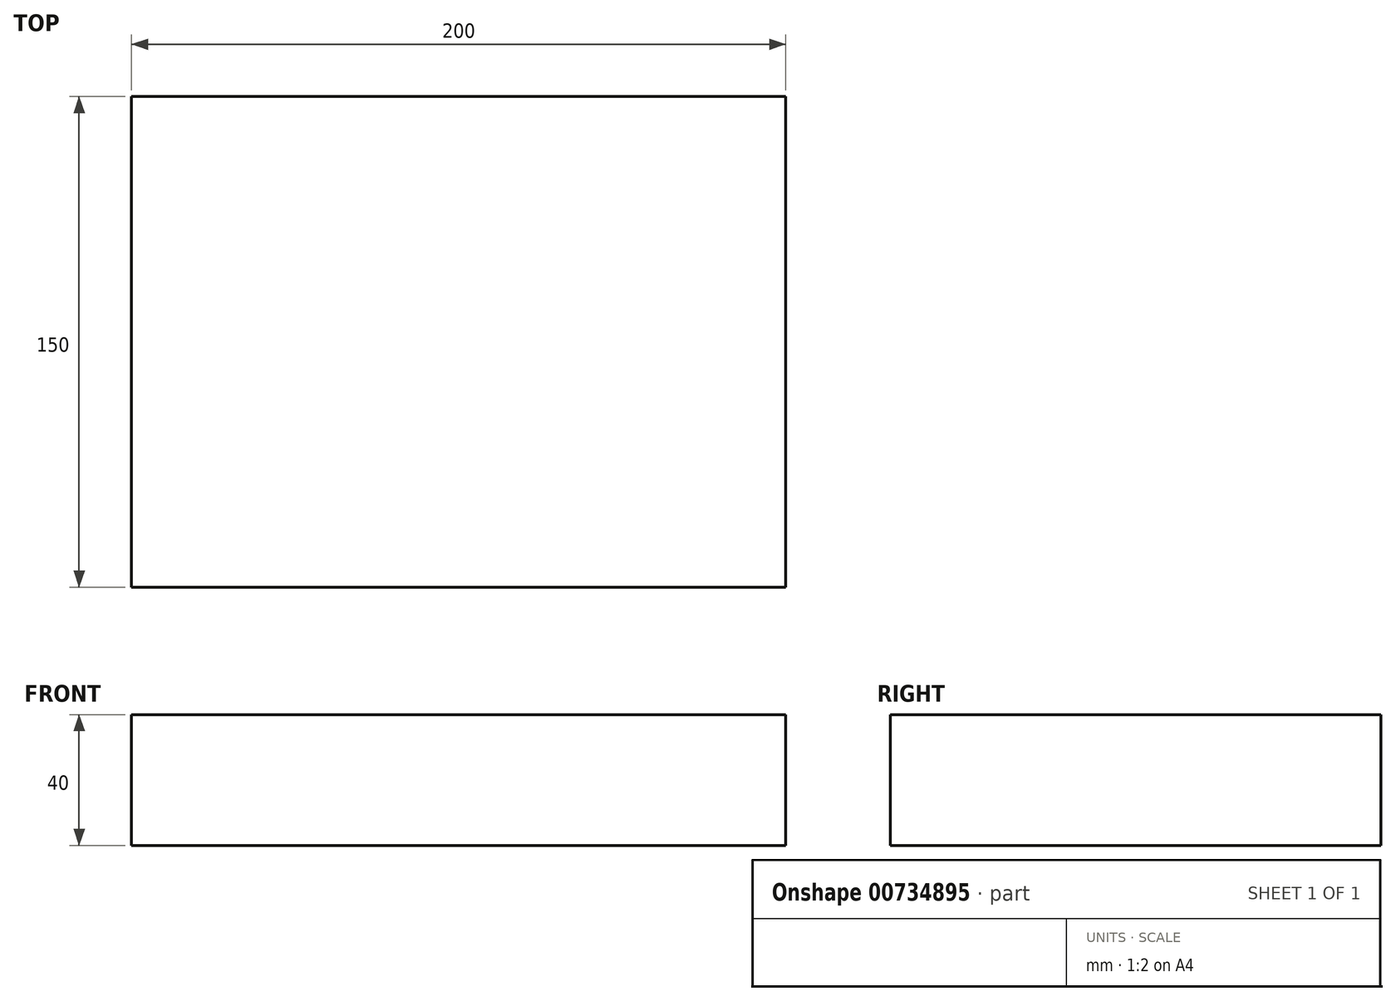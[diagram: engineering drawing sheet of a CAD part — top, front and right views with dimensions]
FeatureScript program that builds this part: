
annotation { "Feature Type Name" : "Feature", "Feature Type Description" : "" }
export const myFeature = defineFeature(function(context is Context, id is Id, definition is map)
    precondition{}
    {
        {
            var Q0;
            Q0=qCreatedBy(makeId("Front.planeOp"),FACE);
            var sketch = newSketch(context, id + "F0", { "sketchPlane" : qUnion([Q0])});
            skLineSegment(sketch, "E0.bottom", {"start": v(-100, 20) * mm, "end": v(100, 20) * mm});
            skLineSegment(sketch, "E0.top", {"start": v(-100, -20) * mm, "end": v(100, -20) * mm});
            skLineSegment(sketch, "E0.left", {"start": v(-100, 20) * mm, "end": v(-100, -20) * mm});
            skLineSegment(sketch, "E0.right", {"start": v(100, 20) * mm, "end": v(100, -20) * mm});
            skPoint(sketch, "E0.middle", {"position": v(0, 0) * mm});
            skSolve(sketch);
        }
        {
            var Q0;
            Q0=makeQuery(id+"F0.imprint","IMPRINT",FACE,{"disambiguationData":[TD([[makeQuery(id+"F0.imprint","IMPRINT",EDGE,{"derivedFrom":sQuery(id+"F0.wireOp",EDGE,"E0.bottom")}),-1.0]])]});
            extrude(context, id + "F1", {"entities" : qUnion([Q0]), "oppositeDirection" : true, "depth" : 150 * mm, "offsetDistance" : 25 * mm});
        }
    });
